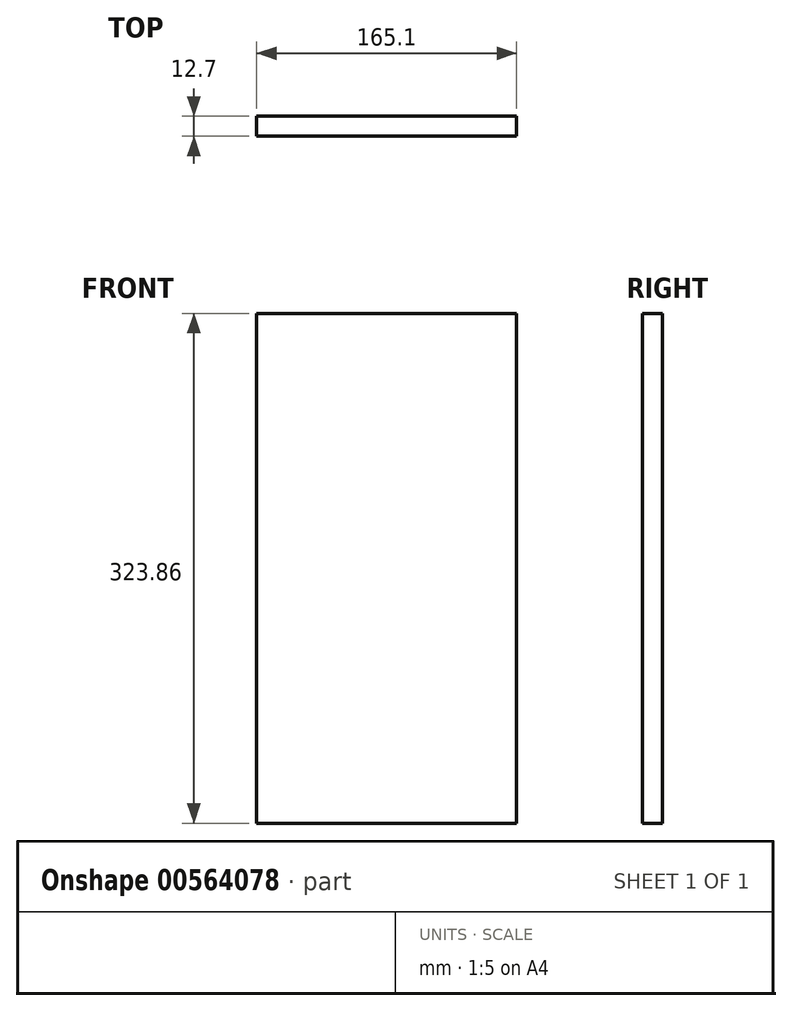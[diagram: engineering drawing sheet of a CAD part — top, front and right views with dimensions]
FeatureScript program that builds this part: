
annotation { "Feature Type Name" : "Feature", "Feature Type Description" : "" }
export const myFeature = defineFeature(function(context is Context, id is Id, definition is map)
    precondition{}
    {
        {
            var Q0;
            Q0=qCreatedBy(makeId("Front.planeOp"),FACE);
            var sketch = newSketch(context, id + "F0", { "sketchPlane" : qUnion([Q0])});
            skLineSegment(sketch, "E0.bottom", {"start": v(-82.55, 161.93) * mm, "end": v(82.55, 161.93) * mm});
            skLineSegment(sketch, "E0.top", {"start": v(-82.55, -161.92) * mm, "end": v(82.55, -161.92) * mm});
            skLineSegment(sketch, "E0.left", {"start": v(-82.55, 161.93) * mm, "end": v(-82.55, -161.92) * mm});
            skLineSegment(sketch, "E0.right", {"start": v(82.55, 161.93) * mm, "end": v(82.55, -161.92) * mm});
            skPoint(sketch, "E0.middle", {"position": v(0, 0) * mm});
            skSolve(sketch);
        }
        {
            var Q0;
            Q0=makeQuery(id+"F0.imprint","IMPRINT",FACE,{"disambiguationData":[TD([[makeQuery(id+"F0.imprint","IMPRINT",EDGE,{"derivedFrom":sQuery(id+"F0.wireOp",EDGE,"E0.bottom")}),-1.0]])]});
            extrude(context, id + "F1", {"entities" : qUnion([Q0]), "endBound" : BoundingType.SYMMETRIC, "depth" : 12.7 * mm, "offsetDistance" : 25.4 * mm});
        }
    });
